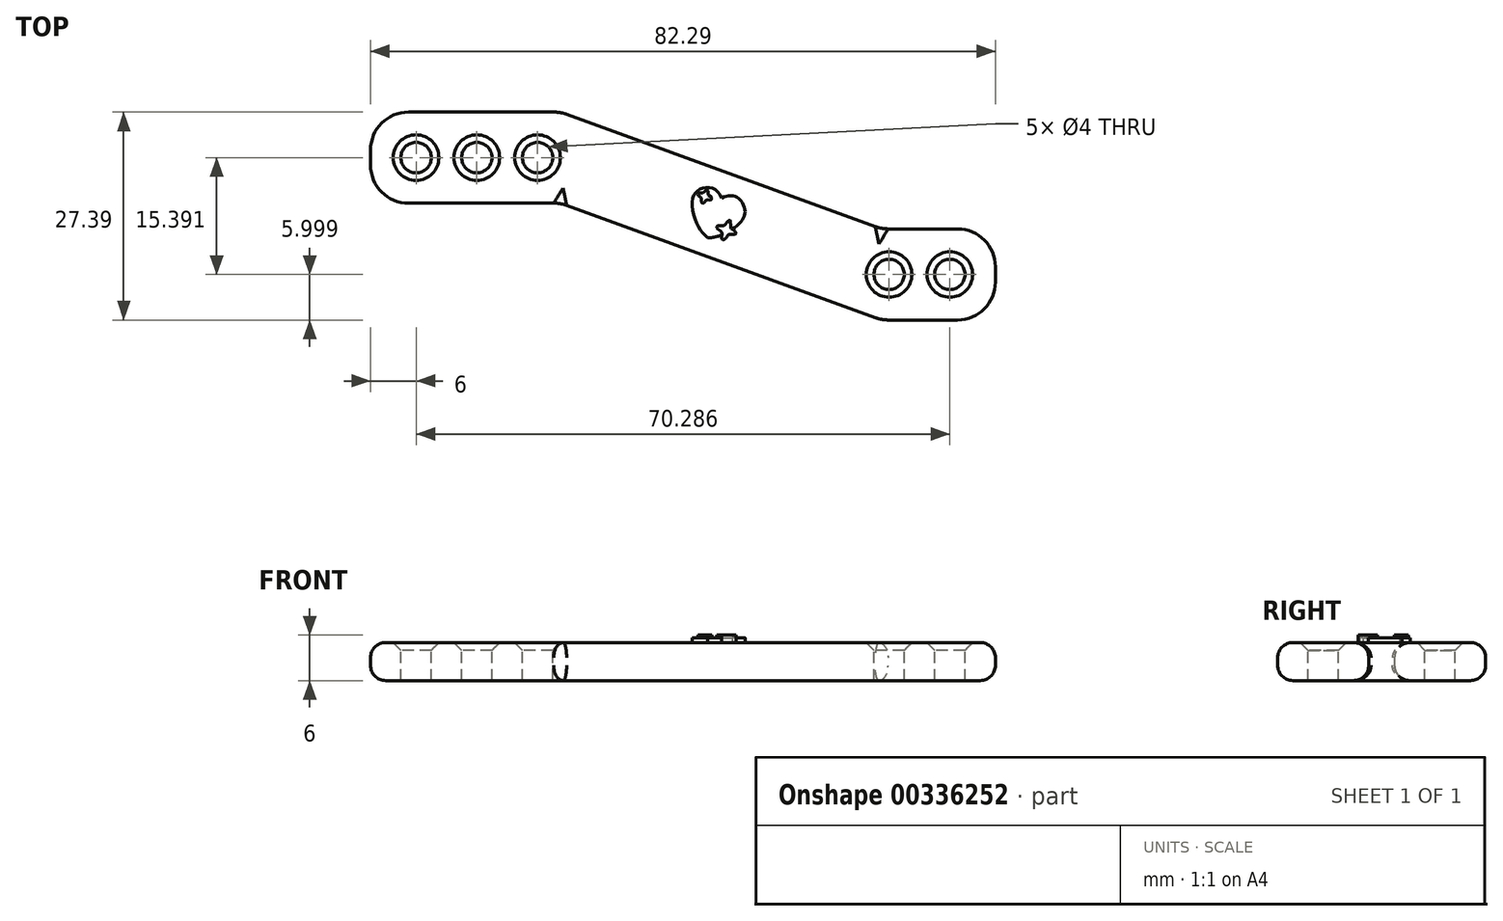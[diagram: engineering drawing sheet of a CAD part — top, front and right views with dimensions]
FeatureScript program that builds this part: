
annotation { "Feature Type Name" : "Feature", "Feature Type Description" : "" }
export const myFeature = defineFeature(function(context is Context, id is Id, definition is map)
    precondition{}
    {
        {
            var Q0;
            Q0=qCreatedBy(makeId("Top.planeOp"),FACE);
            var sketch = newSketch(context, id + "F0", { "sketchPlane" : qUnion([Q0])});
            skLineSegment(sketch, "E0.bottom", {"start": v(0, 12) * mm, "end": v(25, 12) * mm});
            skLineSegment(sketch, "E0.top", {"start": v(0, 0) * mm, "end": v(25, 0) * mm});
            skLineSegment(sketch, "E0.left", {"start": v(0, 12) * mm, "end": v(0, 0) * mm});
            skLineSegment(sketch, "E0.right", {"start": v(25, 12) * mm, "end": v(25, 0) * mm});
            skLineSegment(sketch, "E1.bottom", {"start": v(67.29, -3.4) * mm, "end": v(82.29, -3.4) * mm});
            skLineSegment(sketch, "E1.top", {"start": v(67.29, -15.4) * mm, "end": v(82.29, -15.4) * mm});
            skLineSegment(sketch, "E1.left", {"start": v(67.29, -3.4) * mm, "end": v(67.29, -15.4) * mm});
            skLineSegment(sketch, "E1.right", {"start": v(82.29, -3.4) * mm, "end": v(82.29, -15.4) * mm});
            skLineSegment(sketch, "E2", {"start": v(25, 12) * mm, "end": v(67.29, -3.4) * mm});
            skLineSegment(sketch, "E3", {"start": v(25, 0) * mm, "end": v(67.29, -15.4) * mm});
            skSolve(sketch);
        }
        {
            var Q0;
            Q0=makeQuery(id+"F0.imprint","IMPRINT",FACE,{"disambiguationData":[TD([[makeQuery(id+"F0.imprint","IMPRINT",EDGE,{"derivedFrom":sQuery(id+"F0.wireOp",EDGE,"E0.bottom")}),-1.0]])]});
            var Q1;
            Q1=makeQuery(id+"F0.imprint","IMPRINT",FACE,{"disambiguationData":[TD([[makeQuery(id+"F0.imprint","IMPRINT",EDGE,{"derivedFrom":sQuery(id+"F0.wireOp",EDGE,"E0.right")}),1.0]])]});
            var Q2;
            Q2=makeQuery(id+"F0.imprint","IMPRINT",FACE,{"disambiguationData":[TD([[makeQuery(id+"F0.imprint","IMPRINT",EDGE,{"derivedFrom":sQuery(id+"F0.wireOp",EDGE,"E1.bottom")}),-1.0]])]});
            extrude(context, id + "F1", {"entities" : qUnion([Q0, Q1, Q2]), "depth" : 5 * mm});
        }
        {
            var Q0;
            Q0=makeQuery(id+"F1.opExtrude","CAP_FACE",FACE,{"disambiguationData":[OSD([sQuery(id+"F0.wireOp",EDGE,"E0.bottom"),sQuery(id+"F0.wireOp",EDGE,"E0.top"),sQuery(id+"F0.wireOp",EDGE,"E0.left"),sQuery(id+"F0.wireOp",EDGE,"E1.bottom"),sQuery(id+"F0.wireOp",EDGE,"E1.top"),sQuery(id+"F0.wireOp",EDGE,"E1.right"),sQuery(id+"F0.wireOp",EDGE,"E2"),sQuery(id+"F0.wireOp",EDGE,"E3")])],"isStart":false});
            var sketch = newSketch(context, id + "F2", { "sketchPlane" : qUnion([Q0])});
            skCircle(sketch, "E4", {"center": v(6, 6) * mm, "radius": 2 * mm});
            skCircle(sketch, "E5", {"center": v(76.29, -9.4) * mm, "radius": 2 * mm});
            skCircle(sketch, "E6.1.0.0", {"center": v(14, 6) * mm, "radius": 2 * mm});
            skCircle(sketch, "E6.2.0.0", {"center": v(22, 6) * mm, "radius": 2 * mm});
            skLineSegment(sketch, "E6.direction1", {"start": v(6, 6) * mm, "end": v(14, 6) * mm, "construction": true});
            skCircle(sketch, "E7.1.0.0", {"center": v(68.29, -9.4) * mm, "radius": 2 * mm});
            skLineSegment(sketch, "E7.direction1", {"start": v(76.29, -9.4) * mm, "end": v(68.29, -9.4) * mm, "construction": true});
            skSolve(sketch);
        }
        {
            var Q0;
            Q0=qSketchRegion(id+"F2",true);
            extrude(context, id + "F3", {"entities" : qUnion([Q0]), "operationType" : NewBodyOperationType.REMOVE, "endBound" : BoundingType.THROUGH_ALL, "oppositeDirection" : true, "depth" : 5 * mm});
        }
        {
            var Q0;
            Q0=makeQuery(id+"F1.opExtrude","CAP_EDGE",EDGE,{"disambiguationData":[OSD([sQuery(id+"F0.wireOp",EDGE,"E3")])],"isStart":false});
            var Q1;
            Q1=makeQuery(id+"F1.opExtrude","CAP_EDGE",EDGE,{"disambiguationData":[OSD([sQuery(id+"F0.wireOp",EDGE,"E1.top")])],"isStart":false});
            var Q2;
            Q2=makeQuery(id+"F1.opExtrude","CAP_EDGE",EDGE,{"disambiguationData":[OSD([sQuery(id+"F0.wireOp",EDGE,"E1.right")])],"isStart":false});
            var Q3;
            Q3=makeQuery(id+"F1.opExtrude","CAP_EDGE",EDGE,{"disambiguationData":[OSD([sQuery(id+"F0.wireOp",EDGE,"E1.bottom")])],"isStart":false});
            var Q4;
            Q4=makeQuery(id+"F1.opExtrude","CAP_EDGE",EDGE,{"disambiguationData":[OSD([sQuery(id+"F0.wireOp",EDGE,"E2")])],"isStart":false});
            var Q5;
            Q5=makeQuery(id+"F1.opExtrude","CAP_EDGE",EDGE,{"disambiguationData":[OSD([sQuery(id+"F0.wireOp",EDGE,"E0.bottom")])],"isStart":false});
            var Q6;
            Q6=makeQuery(id+"F1.opExtrude","CAP_EDGE",EDGE,{"disambiguationData":[OSD([sQuery(id+"F0.wireOp",EDGE,"E0.left")])],"isStart":false});
            var Q7;
            Q7=makeQuery(id+"F1.opExtrude","CAP_EDGE",EDGE,{"disambiguationData":[OSD([sQuery(id+"F0.wireOp",EDGE,"E0.top")])],"isStart":false});
            var Q8;
            Q8=makeQuery(id+"F1.opExtrude","CAP_EDGE",EDGE,{"disambiguationData":[OSD([sQuery(id+"F0.wireOp",EDGE,"E3")])],"isStart":true});
            var Q9;
            Q9=makeQuery(id+"F1.opExtrude","CAP_EDGE",EDGE,{"disambiguationData":[OSD([sQuery(id+"F0.wireOp",EDGE,"E1.top")])],"isStart":true});
            var Q10;
            Q10=makeQuery(id+"F1.opExtrude","CAP_EDGE",EDGE,{"disambiguationData":[OSD([sQuery(id+"F0.wireOp",EDGE,"E1.right")])],"isStart":true});
            var Q11;
            Q11=makeQuery(id+"F1.opExtrude","CAP_EDGE",EDGE,{"disambiguationData":[OSD([sQuery(id+"F0.wireOp",EDGE,"E1.bottom")])],"isStart":true});
            var Q12;
            Q12=makeQuery(id+"F1.opExtrude","CAP_EDGE",EDGE,{"disambiguationData":[OSD([sQuery(id+"F0.wireOp",EDGE,"E2")])],"isStart":true});
            var Q13;
            Q13=makeQuery(id+"F1.opExtrude","CAP_EDGE",EDGE,{"disambiguationData":[OSD([sQuery(id+"F0.wireOp",EDGE,"E0.bottom")])],"isStart":true});
            var Q14;
            Q14=makeQuery(id+"F1.opExtrude","CAP_EDGE",EDGE,{"disambiguationData":[OSD([sQuery(id+"F0.wireOp",EDGE,"E0.left")])],"isStart":true});
            var Q15;
            Q15=makeQuery(id+"F1.opExtrude","CAP_EDGE",EDGE,{"disambiguationData":[OSD([sQuery(id+"F0.wireOp",EDGE,"E0.top")])],"isStart":true});
            fillet(context, id + "F4", {"entities" : qUnion([Q0, Q1, Q2, Q3, Q4, Q5, Q6, Q7, Q8, Q9, Q10, Q11, Q12, Q13, Q14, Q15]), "radius" : 2 * mm, "tangentPropagation" : true, "allowEdgeOverflow" : false});
        }
        {
            var Q0;
            Q0=makeQuery(id+"F4.opFillet","BLEND_EDGE",EDGE,{"blendedFrom":[makeQuery(id+"F1.opExtrude","CAP_EDGE",EDGE,{"disambiguationData":[OSD([sQuery(id+"F0.wireOp",EDGE,"E0.top")])],"isStart":false}),makeQuery(id+"F1.opExtrude","CAP_EDGE",EDGE,{"disambiguationData":[OSD([sQuery(id+"F0.wireOp",EDGE,"E0.left")])],"isStart":false})],"blendedInto":[]});
            var Q1;
            Q1=makeQuery(id+"F4.opFillet","BLEND_EDGE",EDGE,{"blendedFrom":[makeQuery(id+"F1.opExtrude","CAP_EDGE",EDGE,{"disambiguationData":[OSD([sQuery(id+"F0.wireOp",EDGE,"E0.top")])],"isStart":false}),makeQuery(id+"F1.opExtrude","CAP_EDGE",EDGE,{"disambiguationData":[OSD([sQuery(id+"F0.wireOp",EDGE,"E3")])],"isStart":false})],"blendedInto":[]});
            var Q2;
            Q2=makeQuery(id+"F4.opFillet","BLEND_EDGE",EDGE,{"blendedFrom":[makeQuery(id+"F1.opExtrude","CAP_EDGE",EDGE,{"disambiguationData":[OSD([sQuery(id+"F0.wireOp",EDGE,"E1.top")])],"isStart":false}),makeQuery(id+"F1.opExtrude","CAP_EDGE",EDGE,{"disambiguationData":[OSD([sQuery(id+"F0.wireOp",EDGE,"E3")])],"isStart":false})],"blendedInto":[]});
            var Q3;
            Q3=makeQuery(id+"F4.opFillet","BLEND_EDGE",EDGE,{"blendedFrom":[makeQuery(id+"F1.opExtrude","CAP_EDGE",EDGE,{"disambiguationData":[OSD([sQuery(id+"F0.wireOp",EDGE,"E1.top")])],"isStart":false}),makeQuery(id+"F1.opExtrude","CAP_EDGE",EDGE,{"disambiguationData":[OSD([sQuery(id+"F0.wireOp",EDGE,"E1.right")])],"isStart":false})],"blendedInto":[]});
            var Q4;
            Q4=makeQuery(id+"F4.opFillet","BLEND_EDGE",EDGE,{"blendedFrom":[makeQuery(id+"F1.opExtrude","CAP_EDGE",EDGE,{"disambiguationData":[OSD([sQuery(id+"F0.wireOp",EDGE,"E1.bottom")])],"isStart":false}),makeQuery(id+"F1.opExtrude","CAP_EDGE",EDGE,{"disambiguationData":[OSD([sQuery(id+"F0.wireOp",EDGE,"E1.right")])],"isStart":false})],"blendedInto":[]});
            var Q5;
            Q5=makeQuery(id+"F4.opFillet","BLEND_EDGE",EDGE,{"blendedFrom":[makeQuery(id+"F1.opExtrude","CAP_EDGE",EDGE,{"disambiguationData":[OSD([sQuery(id+"F0.wireOp",EDGE,"E1.bottom")])],"isStart":false}),makeQuery(id+"F1.opExtrude","CAP_EDGE",EDGE,{"disambiguationData":[OSD([sQuery(id+"F0.wireOp",EDGE,"E2")])],"isStart":false})],"blendedInto":[]});
            var Q6;
            Q6=makeQuery(id+"F4.opFillet","BLEND_EDGE",EDGE,{"blendedFrom":[makeQuery(id+"F1.opExtrude","CAP_EDGE",EDGE,{"disambiguationData":[OSD([sQuery(id+"F0.wireOp",EDGE,"E0.bottom")])],"isStart":false}),makeQuery(id+"F1.opExtrude","CAP_EDGE",EDGE,{"disambiguationData":[OSD([sQuery(id+"F0.wireOp",EDGE,"E2")])],"isStart":false})],"blendedInto":[]});
            var Q7;
            Q7=makeQuery(id+"F4.opFillet","BLEND_EDGE",EDGE,{"blendedFrom":[makeQuery(id+"F1.opExtrude","CAP_EDGE",EDGE,{"disambiguationData":[OSD([sQuery(id+"F0.wireOp",EDGE,"E0.bottom")])],"isStart":false}),makeQuery(id+"F1.opExtrude","CAP_EDGE",EDGE,{"disambiguationData":[OSD([sQuery(id+"F0.wireOp",EDGE,"E0.left")])],"isStart":false})],"blendedInto":[]});
            fillet(context, id + "F5", {"entities" : qUnion([Q0, Q1, Q2, Q3, Q4, Q5, Q6, Q7]), "radius" : 5 * mm, "tangentPropagation" : true, "allowEdgeOverflow" : false});
        }
        {
            var Q0;
            Q0=makeQuery(id+"F1.opExtrude","CAP_FACE",FACE,{"disambiguationData":[OSD([sQuery(id+"F0.wireOp",EDGE,"E0.bottom"),sQuery(id+"F0.wireOp",EDGE,"E0.top"),sQuery(id+"F0.wireOp",EDGE,"E0.left"),sQuery(id+"F0.wireOp",EDGE,"E1.bottom"),sQuery(id+"F0.wireOp",EDGE,"E1.top"),sQuery(id+"F0.wireOp",EDGE,"E1.right"),sQuery(id+"F0.wireOp",EDGE,"E2"),sQuery(id+"F0.wireOp",EDGE,"E3")])],"isStart":false});
            chamfer(context, id + "F6", {"entities" : qUnion([Q0]), "width" : 1 * mm, "tangentPropagation" : true});
        }
        {
            var Q0;
            Q0=makeQuery(id+"F1.opExtrude","CAP_FACE",FACE,{"disambiguationData":[OSD([sQuery(id+"F0.wireOp",EDGE,"E0.bottom"),sQuery(id+"F0.wireOp",EDGE,"E0.top"),sQuery(id+"F0.wireOp",EDGE,"E0.left"),sQuery(id+"F0.wireOp",EDGE,"E1.bottom"),sQuery(id+"F0.wireOp",EDGE,"E1.top"),sQuery(id+"F0.wireOp",EDGE,"E1.right"),sQuery(id+"F0.wireOp",EDGE,"E2"),sQuery(id+"F0.wireOp",EDGE,"E3")])],"isStart":false});
            var sketch = newSketch(context, id + "F7", { "sketchPlane" : qUnion([Q0])});
            skFitSpline(sketch, "E8", {"points": [v(46.25, 0.67) * mm, v(48.13, 0.83) * mm, v(49.3, -0.9) * mm, v(48.6, -2.64) * mm, v(45.9, -4.3) * mm, v(44.38, -4.59) * mm], "startDerivative": vector(9.88, 5.2) * mm, "endDerivative": vector(-8.03, -0.61) * mm});
            skFitSpline(sketch, "E9", {"points": [v(46.25, 0.67) * mm, v(44.86, 2) * mm, v(43.2, 1.73) * mm, v(42.4, 0.42) * mm, v(42.95, -2.64) * mm, v(44.38, -4.59) * mm], "startDerivative": vector(-4.82, 11.23) * mm, "endDerivative": vector(7.62, -7.18) * mm});
            skFitSpline(sketch, "E10", {"points": [v(46.56, -2.92) * mm, v(47.31, -2.24) * mm, v(47.45, -3.23) * mm, v(47.74, -3.53) * mm, v(48.11, -4.01) * mm, v(47.17, -4.13) * mm, v(46.9, -4.46) * mm, v(46.37, -4.81) * mm, v(46.25, -4.35) * mm, v(46.25, -3.86) * mm, v(45.7, -3.33) * mm, v(45.59, -3.06) * mm, v(46, -2.95) * mm, v(46.56, -2.92) * mm]});
            skFitSpline(sketch, "E11", {"points": [v(43.78, 1.33) * mm, v(44.17, 1.73) * mm, v(44.3, 1.79) * mm, v(44.47, 1.56) * mm, v(44.48, 1.11) * mm, v(44.91, 0.7) * mm, v(44.9, 0.52) * mm, v(44.73, 0.41) * mm, v(44.28, 0.44) * mm, v(43.93, 0.04) * mm, v(43.7, -0.03) * mm, v(43.56, 0.22) * mm, v(43.57, 0.65) * mm, v(43.2, 0.96) * mm, v(43.1, 1.2) * mm, v(43.26, 1.35) * mm, v(43.78, 1.33) * mm]});
            skSolve(sketch);
        }
        {
            var Q0;
            Q0=makeQuery(id+"F7.imprint","IMPRINT",FACE,{"disambiguationData":[TD([[makeQuery(id+"F7.imprint","IMPRINT",EDGE,{"derivedFrom":sQuery(id+"F7.wireOp",EDGE,"E11")}),-1.0]])]});
            var Q1;
            {var subQ0=sQuery(id+"F7.wireOp",EDGE,"E10");var subQ1=sQuery(id+"F7.wireOp",EDGE,"E8");var subQ2=makeQuery(id+"F7.imprint","INTERSECT",VERTEX,{"disambiguationData":[OD(0.0)],"derivedFrom":[subQ1,subQ0]});Q1=makeQuery(id+"F7.imprint","IMPRINT",FACE,{"disambiguationData":[TD([[makeQuery(id+"F7.imprint","IMPRINT",EDGE,{"disambiguationData":[TD([[subQ2,-1.0]])],"derivedFrom":subQ1}),1.0]])]});}
            var Q2;
            {var subQ0=sQuery(id+"F7.wireOp",EDGE,"E10");var subQ1=sQuery(id+"F7.wireOp",EDGE,"E8");var subQ2=makeQuery(id+"F7.imprint","INTERSECT",VERTEX,{"disambiguationData":[OD(0.0)],"derivedFrom":[subQ1,subQ0]});Q2=makeQuery(id+"F7.imprint","IMPRINT",FACE,{"disambiguationData":[TD([[makeQuery(id+"F7.imprint","IMPRINT",EDGE,{"disambiguationData":[TD([[subQ2,-1.0]])],"derivedFrom":subQ1}),-1.0]])]});}
            extrude(context, id + "F8", {"entities" : qUnion([Q0, Q1, Q2]), "operationType" : NewBodyOperationType.ADD, "depth" : 1 * mm});
        }
        {
            var Q0;
            Q0 = qSketchRegion(id + "F7", true);
            extrude(context, id + "F9", {"entities" : qUnion([Q0]), "operationType" : NewBodyOperationType.ADD, "depth" : .65 * mm});
        }
    });
